# Revit family: Roller_Shades-Lutron-Contract_Dual_Roller_Motorized-02
name_source: partatom
category: Specialty Equipment
revit_build: Autodesk Revit 2017 (Build: 20160225_1515(x64)
units: mm (PartAtom-declared; Revit-internal decimal feet)

## family parameters
Cut with Voids When Loaded = No
Host = Face
OmniClass Number = 23.30.60.14.21
OmniClass Title = Shades
Part Type = Normal
Room Calculation Point = No
Round Connector Dimension = Use Diameter
Shared = No

## types (3) — shared parameters
Assembly Code = E2010320
Default Elevation = 0' - 0"
Description = Motorized Roller Shade
Finish = Finish - Lutron - White
Instruction Sheet Link = http://www.lutron.com
Light Gap = 0' - 0 3/4"
Load Classification = Other
Manufacturer = Lutron Electronics Co., Inc
Manufacturer Fax Number = 610-282-1243
Model = Motorized Shade
Number of Poles = 1
Performance URL = http://www.lutron.com
Power Factor = 1
Product Documentation Link = http://www.lutron.com
Product Name = Contract Roller - Dual Motorized Shade
Product Page URL = http://www.lutron.com
Series = Contract Roller Shades
Shade Material = Fabric - Lutron - Linen - White
URL = http://www.lutron.com
Version = 2017 - v1.0b
Video Link = https://www.youtube.com
Warranty URL = http://www.lutron.com
zero-valued in all types: Cost

## per-type parameters (varying)
| type | Apparent Load | Fixture Angle | Pocket Inset | Voltage |
| Ceiling Mount | 35 VA | 0.00° | 0' - 0" | 35 V |
| Wall Mount | 0 VA | 90.00° | 0' - 0" | 0 V |
| Pocket Mount | 0 VA | 0.00° | 0' - 11" | 0 V |

note: column(s) folded — value = type name in every type: Mounting

type visibility flags (boolean, named after types; folded from table):
- Ceiling Mount: Yes: Ceiling Mount
- Wall Mount: Yes: Wall Mount
- Pocket Mount: Yes: Ceiling Mount, Pocket Mount Enclosure

## geometry (parser evidence)
native form markers: Blend x2, Sweep x13
no freeform markers — native parametric forms only
